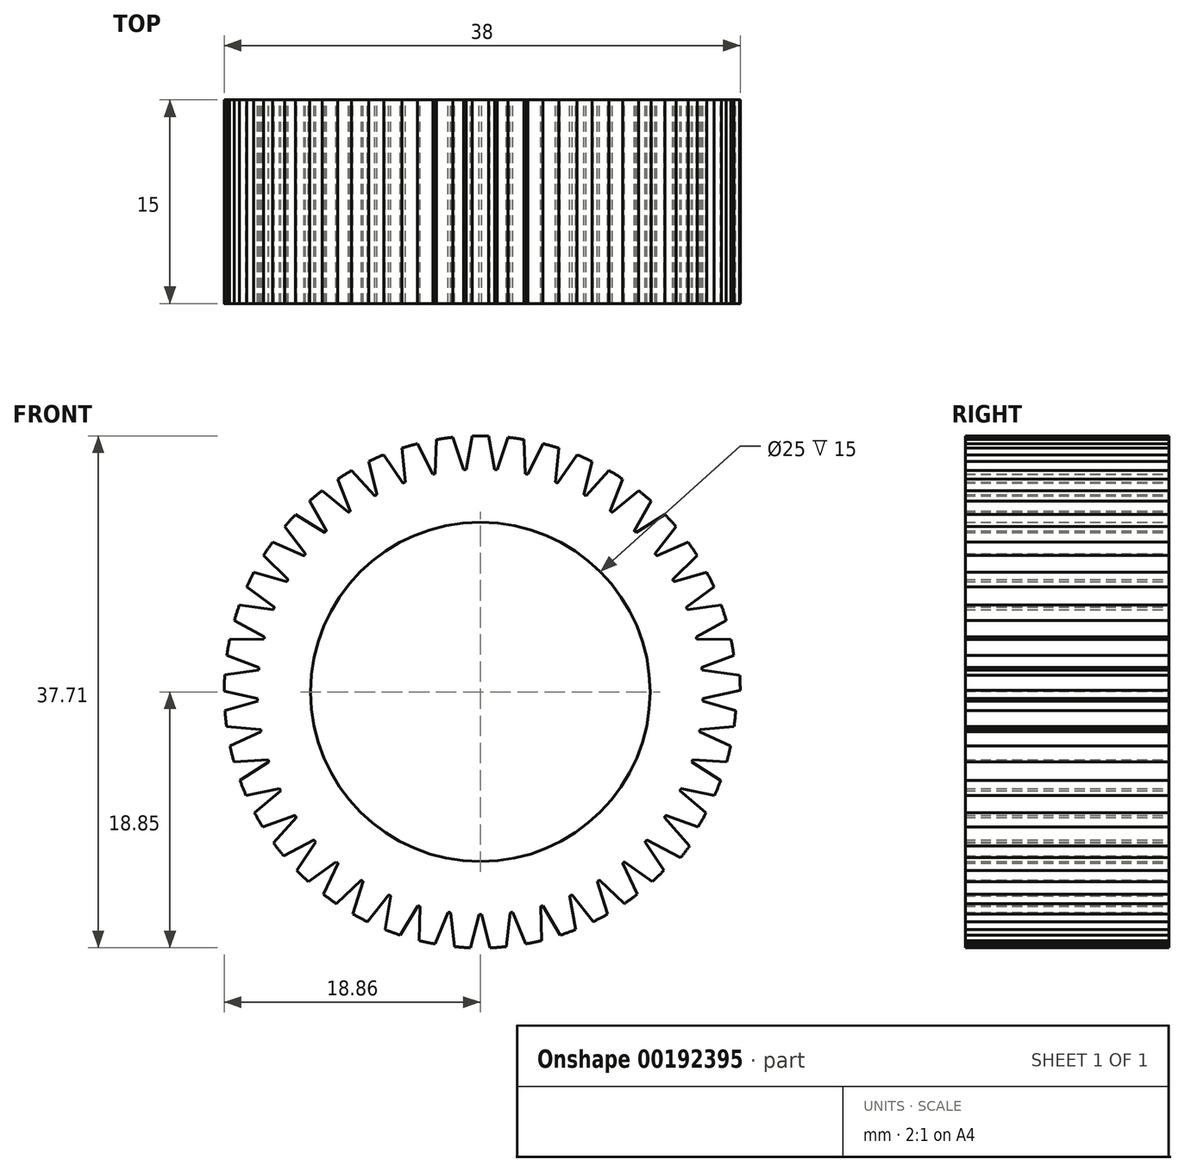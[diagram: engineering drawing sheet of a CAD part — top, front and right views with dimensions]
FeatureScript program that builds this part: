
annotation { "Feature Type Name" : "Feature", "Feature Type Description" : "" }
export const myFeature = defineFeature(function(context is Context, id is Id, definition is map)
    precondition{}
    {
        {
            var Q0;
            Q0=qCreatedBy(makeId("Front.planeOp"),FACE);
            var sketch = newSketch(context, id + "F0", { "sketchPlane" : qUnion([Q0])});
            skCircle(sketch, "E0", {"center": v(0, 0) * mm, "radius": 12.5 * mm});
            skLineSegment(sketch, "E1", {"start": v(-0.6, 18.85) * mm, "end": v(-1.05, 16.37) * mm});
            skLineSegment(sketch, "E2.MirrorCS", {"start": v(0.6, 18.85) * mm, "end": v(1.05, 16.37) * mm});
            skCircle(sketch, "E3", {"center": v(0, 0) * mm, "radius": 16.4 * mm});
            skLineSegment(sketch, "E4.1.1", {"start": v(-3.22, 18.58) * mm, "end": v(-3.32, 16.07) * mm});
            skLineSegment(sketch, "E4.1.2", {"start": v(-2.03, 18.75) * mm, "end": v(-1.23, 16.36) * mm});
            skLineSegment(sketch, "E4.2.1", {"start": v(-5.77, 17.96) * mm, "end": v(-5.53, 15.45) * mm});
            skLineSegment(sketch, "E4.2.2", {"start": v(-4.62, 18.29) * mm, "end": v(-3.5, 16.03) * mm});
            skLineSegment(sketch, "E5.4.3.0", {"start": v(-8.21, 16.98) * mm, "end": v(-7.62, 14.53) * mm});
            skLineSegment(sketch, "E5.7.3.0", {"start": v(-7.12, 17.46) * mm, "end": v(-5.7, 15.39) * mm});
            skLineSegment(sketch, "E5.4.4.0", {"start": v(-10.5, 15.67) * mm, "end": v(-9.57, 13.33) * mm});
            skLineSegment(sketch, "E5.7.4.0", {"start": v(-9.48, 16.3) * mm, "end": v(-7.78, 14.44) * mm});
            skLineSegment(sketch, "E5.4.5.0", {"start": v(-12.58, 14.06) * mm, "end": v(-11.33, 11.86) * mm});
            skLineSegment(sketch, "E5.7.5.0", {"start": v(-11.66, 14.83) * mm, "end": v(-9.72, 13.22) * mm});
            skLineSegment(sketch, "E5.4.6.0", {"start": v(-14.4, 12.17) * mm, "end": v(-12.87, 10.17) * mm});
            skLineSegment(sketch, "E5.7.6.0", {"start": v(-13.6, 13.06) * mm, "end": v(-11.46, 11.74) * mm});
            skLineSegment(sketch, "E5.4.7.0", {"start": v(-15.96, 10.04) * mm, "end": v(-14.16, 8.28) * mm});
            skLineSegment(sketch, "E5.7.7.0", {"start": v(-15.3, 11.04) * mm, "end": v(-12.98, 10.03) * mm});
            skLineSegment(sketch, "E5.4.8.0", {"start": v(-17.2, 7.73) * mm, "end": v(-15.18, 6.23) * mm});
            skLineSegment(sketch, "E5.7.8.0", {"start": v(-16.68, 8.8) * mm, "end": v(-14.25, 8.12) * mm});
            skLineSegment(sketch, "E5.4.9.0", {"start": v(-18.11, 5.26) * mm, "end": v(-15.9, 4.06) * mm});
            skLineSegment(sketch, "E5.7.9.0", {"start": v(-17.74, 6.4) * mm, "end": v(-15.25, 6.06) * mm});
            skLineSegment(sketch, "E5.4.10.0", {"start": v(-18.67, 2.68) * mm, "end": v(-16.3, 1.8) * mm});
            skLineSegment(sketch, "E5.7.10.0", {"start": v(-18.46, 3.86) * mm, "end": v(-15.94, 3.88) * mm});
            skLineSegment(sketch, "E5.4.11.0", {"start": v(-18.86, 0.06) * mm, "end": v(-16.4, -0.48) * mm});
            skLineSegment(sketch, "E5.7.11.0", {"start": v(-18.82, 1.26) * mm, "end": v(-16.33, 1.62) * mm});
            skLineSegment(sketch, "E5.4.12.0", {"start": v(-18.69, -2.57) * mm, "end": v(-16.17, -2.76) * mm});
            skLineSegment(sketch, "E5.7.12.0", {"start": v(-18.81, -1.38) * mm, "end": v(-16.4, -0.66) * mm});
            skLineSegment(sketch, "E5.4.13.0", {"start": v(-18.15, -5.14) * mm, "end": v(-15.63, -4.98) * mm});
            skLineSegment(sketch, "E5.7.13.0", {"start": v(-18.44, -3.98) * mm, "end": v(-16.14, -2.94) * mm});
            skLineSegment(sketch, "E5.4.14.0", {"start": v(-17.25, -7.62) * mm, "end": v(-14.79, -7.11) * mm});
            skLineSegment(sketch, "E5.7.14.0", {"start": v(-17.7, -6.5) * mm, "end": v(-15.58, -5.16) * mm});
            skLineSegment(sketch, "E5.4.15.0", {"start": v(-16.03, -9.94) * mm, "end": v(-13.65, -9.1) * mm});
            skLineSegment(sketch, "E5.7.15.0", {"start": v(-16.62, -8.9) * mm, "end": v(-14.7, -7.27) * mm});
            skLineSegment(sketch, "E5.4.16.0", {"start": v(-14.49, -12.08) * mm, "end": v(-12.25, -10.91) * mm});
            skLineSegment(sketch, "E5.7.16.0", {"start": v(-15.22, -11.13) * mm, "end": v(-13.55, -9.25) * mm});
            skLineSegment(sketch, "E5.4.17.0", {"start": v(-12.66, -13.98) * mm, "end": v(-10.62, -12.5) * mm});
            skLineSegment(sketch, "E5.7.17.0", {"start": v(-13.53, -13.14) * mm, "end": v(-12.13, -11.05) * mm});
            skLineSegment(sketch, "E5.4.18.0", {"start": v(-10.6, -15.6) * mm, "end": v(-8.77, -13.87) * mm});
            skLineSegment(sketch, "E5.7.18.0", {"start": v(-11.56, -14.9) * mm, "end": v(-10.48, -12.63) * mm});
            skLineSegment(sketch, "E5.4.19.0", {"start": v(-8.32, -16.93) * mm, "end": v(-6.76, -14.95) * mm});
            skLineSegment(sketch, "E5.7.19.0", {"start": v(-9.38, -16.36) * mm, "end": v(-8.62, -13.96) * mm});
            skLineSegment(sketch, "E6.4.20.0", {"start": v(-5.88, -17.92) * mm, "end": v(-4.6, -15.75) * mm});
            skLineSegment(sketch, "E6.7.20.0", {"start": v(-7, -17.5) * mm, "end": v(-6.6, -15.02) * mm});
            skLineSegment(sketch, "E6.4.21.0", {"start": v(-3.33, -18.56) * mm, "end": v(-2.37, -16.23) * mm});
            skLineSegment(sketch, "E6.7.21.0", {"start": v(-4.5, -18.31) * mm, "end": v(-4.43, -15.8) * mm});
            skLineSegment(sketch, "E6.4.22.0", {"start": v(-0.72, -18.85) * mm, "end": v(-0.1, -16.4) * mm});
            skLineSegment(sketch, "E6.7.22.0", {"start": v(-1.91, -18.76) * mm, "end": v(-2.2, -16.26) * mm});
            skLineSegment(sketch, "E6.4.23.0", {"start": v(1.91, -18.76) * mm, "end": v(2.2, -16.26) * mm});
            skLineSegment(sketch, "E6.7.23.0", {"start": v(0.72, -18.85) * mm, "end": v(0.1, -16.4) * mm});
            skLineSegment(sketch, "E6.4.24.0", {"start": v(4.5, -18.31) * mm, "end": v(4.43, -15.8) * mm});
            skLineSegment(sketch, "E6.7.24.0", {"start": v(3.33, -18.56) * mm, "end": v(2.37, -16.23) * mm});
            skLineSegment(sketch, "E6.4.25.0", {"start": v(7, -17.5) * mm, "end": v(6.6, -15.02) * mm});
            skLineSegment(sketch, "E6.7.25.0", {"start": v(5.88, -17.92) * mm, "end": v(4.6, -15.75) * mm});
            skLineSegment(sketch, "E6.4.26.0", {"start": v(9.38, -16.36) * mm, "end": v(8.62, -13.96) * mm});
            skLineSegment(sketch, "E6.7.26.0", {"start": v(8.32, -16.93) * mm, "end": v(6.76, -14.95) * mm});
            skLineSegment(sketch, "E6.4.27.0", {"start": v(11.56, -14.9) * mm, "end": v(10.48, -12.63) * mm});
            skLineSegment(sketch, "E6.7.27.0", {"start": v(10.6, -15.6) * mm, "end": v(8.77, -13.87) * mm});
            skLineSegment(sketch, "E6.4.28.0", {"start": v(13.53, -13.14) * mm, "end": v(12.13, -11.05) * mm});
            skLineSegment(sketch, "E6.7.28.0", {"start": v(12.66, -13.98) * mm, "end": v(10.62, -12.5) * mm});
            skArc(sketch, "E6.1.29.0", {"start": v(14.74, -12.21) * mm, "mid": v(15.08, -11.78) * mm, "end": v(15.41, -11.35) * mm});
            skLineSegment(sketch, "E6.4.29.0", {"start": v(15.41, -11.35) * mm, "end": v(13.55, -9.25) * mm});
            skLineSegment(sketch, "E6.7.29.0", {"start": v(14.74, -12.21) * mm, "end": v(12.25, -10.91) * mm});
            skLineSegment(sketch, "E6.4.30.0", {"start": v(16.62, -8.9) * mm, "end": v(14.7, -7.27) * mm});
            skLineSegment(sketch, "E6.7.30.0", {"start": v(16.03, -9.94) * mm, "end": v(13.65, -9.1) * mm});
            skLineSegment(sketch, "E6.4.31.0", {"start": v(17.7, -6.5) * mm, "end": v(15.58, -5.16) * mm});
            skLineSegment(sketch, "E6.7.31.0", {"start": v(17.25, -7.62) * mm, "end": v(14.79, -7.11) * mm});
            skLineSegment(sketch, "E6.4.32.0", {"start": v(18.44, -3.98) * mm, "end": v(16.14, -2.94) * mm});
            skLineSegment(sketch, "E6.7.32.0", {"start": v(18.15, -5.14) * mm, "end": v(15.63, -4.98) * mm});
            skLineSegment(sketch, "E6.4.33.0", {"start": v(18.81, -1.38) * mm, "end": v(16.4, -0.66) * mm});
            skLineSegment(sketch, "E6.7.33.0", {"start": v(18.69, -2.57) * mm, "end": v(16.17, -2.76) * mm});
            skArc(sketch, "E6.1.34.0", {"start": v(19.14, 0.12) * mm, "mid": v(19.13, 0.67) * mm, "end": v(19.1, 1.21) * mm});
            skLineSegment(sketch, "E6.4.34.0", {"start": v(19.1, 1.21) * mm, "end": v(16.33, 1.62) * mm});
            skLineSegment(sketch, "E6.7.34.0", {"start": v(19.14, 0.12) * mm, "end": v(16.4, -0.48) * mm});
            skLineSegment(sketch, "E6.4.35.0", {"start": v(18.46, 3.86) * mm, "end": v(15.94, 3.88) * mm});
            skLineSegment(sketch, "E6.7.35.0", {"start": v(18.67, 2.68) * mm, "end": v(16.3, 1.8) * mm});
            skLineSegment(sketch, "E6.4.36.0", {"start": v(17.74, 6.4) * mm, "end": v(15.25, 6.06) * mm});
            skLineSegment(sketch, "E6.7.36.0", {"start": v(18.11, 5.26) * mm, "end": v(15.9, 4.06) * mm});
            skLineSegment(sketch, "E6.4.37.0", {"start": v(16.68, 8.8) * mm, "end": v(14.25, 8.12) * mm});
            skLineSegment(sketch, "E6.7.37.0", {"start": v(17.2, 7.73) * mm, "end": v(15.18, 6.23) * mm});
            skLineSegment(sketch, "E6.4.38.0", {"start": v(15.3, 11.04) * mm, "end": v(12.98, 10.03) * mm});
            skLineSegment(sketch, "E6.7.38.0", {"start": v(15.96, 10.04) * mm, "end": v(14.16, 8.28) * mm});
            skLineSegment(sketch, "E6.4.39.0", {"start": v(13.6, 13.06) * mm, "end": v(11.46, 11.74) * mm});
            skLineSegment(sketch, "E6.7.39.0", {"start": v(14.4, 12.17) * mm, "end": v(12.87, 10.17) * mm});
            skLineSegment(sketch, "E6.4.40.0", {"start": v(11.66, 14.83) * mm, "end": v(9.72, 13.22) * mm});
            skLineSegment(sketch, "E6.7.40.0", {"start": v(12.58, 14.06) * mm, "end": v(11.33, 11.86) * mm});
            skLineSegment(sketch, "E6.4.41.0", {"start": v(9.48, 16.3) * mm, "end": v(7.78, 14.44) * mm});
            skLineSegment(sketch, "E6.7.41.0", {"start": v(10.5, 15.67) * mm, "end": v(9.57, 13.33) * mm});
            skLineSegment(sketch, "E6.4.42.0", {"start": v(7.12, 17.46) * mm, "end": v(5.7, 15.39) * mm});
            skLineSegment(sketch, "E6.7.42.0", {"start": v(8.21, 16.98) * mm, "end": v(7.62, 14.53) * mm});
            skLineSegment(sketch, "E6.4.43.0", {"start": v(4.62, 18.29) * mm, "end": v(3.5, 16.03) * mm});
            skLineSegment(sketch, "E6.7.43.0", {"start": v(5.77, 17.96) * mm, "end": v(5.53, 15.45) * mm});
            skLineSegment(sketch, "E6.4.44.0", {"start": v(2.03, 18.75) * mm, "end": v(1.23, 16.36) * mm});
            skLineSegment(sketch, "E6.7.44.0", {"start": v(3.22, 18.58) * mm, "end": v(3.32, 16.07) * mm});
            skArc(sketch, "E7", {"start": v(-9.48, 16.3) * mm, "mid": v(-10, 16) * mm, "end": v(-10.5, 15.67) * mm});
            skArc(sketch, "E8.trimOffspring", {"start": v(-11.66, 14.83) * mm, "mid": v(-12.12, 14.45) * mm, "end": v(-12.58, 14.06) * mm});
            skArc(sketch, "E9.trimOffspring", {"start": v(-13.6, 13.06) * mm, "mid": v(-14.02, 12.62) * mm, "end": v(-14.4, 12.17) * mm});
            skArc(sketch, "E10.trimOffspring", {"start": v(-15.3, 11.04) * mm, "mid": v(-15.64, 10.55) * mm, "end": v(-15.96, 10.04) * mm});
            skArc(sketch, "E11.trimOffspring", {"start": v(-16.68, 8.8) * mm, "mid": v(-16.95, 8.27) * mm, "end": v(-17.2, 7.73) * mm});
            skArc(sketch, "E12.trimOffspring", {"start": v(-17.74, 6.4) * mm, "mid": v(-17.94, 5.83) * mm, "end": v(-18.11, 5.26) * mm});
            skArc(sketch, "E13.trimOffspring", {"start": v(-18.46, 3.86) * mm, "mid": v(-18.57, 3.28) * mm, "end": v(-18.67, 2.68) * mm});
            skArc(sketch, "E14.trimOffspring", {"start": v(-18.82, 1.26) * mm, "mid": v(-18.85, 0.66) * mm, "end": v(-18.86, 0.06) * mm});
            skArc(sketch, "E15.trimOffspring", {"start": v(-18.81, -1.38) * mm, "mid": v(-18.76, -1.97) * mm, "end": v(-18.69, -2.57) * mm});
            skArc(sketch, "E16.trimOffspring", {"start": v(-18.44, -3.98) * mm, "mid": v(-18.3, -4.56) * mm, "end": v(-18.15, -5.14) * mm});
            skArc(sketch, "E17.trimOffspring", {"start": v(-17.7, -6.5) * mm, "mid": v(-17.49, -7.07) * mm, "end": v(-17.25, -7.62) * mm});
            skArc(sketch, "E18.trimOffspring", {"start": v(-16.62, -8.9) * mm, "mid": v(-16.33, -9.43) * mm, "end": v(-16.03, -9.94) * mm});
            skArc(sketch, "E19.trimOffspring", {"start": v(-15.22, -11.13) * mm, "mid": v(-14.86, -11.61) * mm, "end": v(-14.49, -12.08) * mm});
            skArc(sketch, "E20.trimOffspring", {"start": v(-13.53, -13.14) * mm, "mid": v(-13.1, -13.57) * mm, "end": v(-12.66, -13.98) * mm});
            skArc(sketch, "E21.trimOffspring", {"start": v(-11.56, -14.9) * mm, "mid": v(-11.09, -15.26) * mm, "end": v(-10.6, -15.6) * mm});
            skArc(sketch, "E22.trimOffspring", {"start": v(-9.38, -16.36) * mm, "mid": v(-8.85, -16.65) * mm, "end": v(-8.32, -16.93) * mm});
            skArc(sketch, "E23.trimOffspring", {"start": v(-7, -17.5) * mm, "mid": v(-6.45, -17.72) * mm, "end": v(-5.88, -17.92) * mm});
            skArc(sketch, "E24.trimOffspring", {"start": v(-4.5, -18.31) * mm, "mid": v(-3.92, -18.45) * mm, "end": v(-3.33, -18.56) * mm});
            skArc(sketch, "E25.trimOffspring", {"start": v(-1.91, -18.76) * mm, "mid": v(-1.32, -18.81) * mm, "end": v(-0.72, -18.85) * mm});
            skArc(sketch, "E26.trimOffspring", {"start": v(0.72, -18.85) * mm, "mid": v(1.32, -18.81) * mm, "end": v(1.91, -18.76) * mm});
            skArc(sketch, "E27.trimOffspring", {"start": v(3.33, -18.56) * mm, "mid": v(3.92, -18.45) * mm, "end": v(4.5, -18.31) * mm});
            skArc(sketch, "E28.trimOffspring", {"start": v(5.88, -17.92) * mm, "mid": v(6.45, -17.72) * mm, "end": v(7, -17.5) * mm});
            skArc(sketch, "E29.trimOffspring", {"start": v(8.32, -16.93) * mm, "mid": v(8.85, -16.65) * mm, "end": v(9.38, -16.36) * mm});
            skArc(sketch, "E30.trimOffspring", {"start": v(10.6, -15.6) * mm, "mid": v(11.09, -15.26) * mm, "end": v(11.56, -14.9) * mm});
            skArc(sketch, "E31.trimOffspring", {"start": v(12.66, -13.98) * mm, "mid": v(13.1, -13.57) * mm, "end": v(13.53, -13.14) * mm});
            skArc(sketch, "E32.trimOffspring", {"start": v(16.03, -9.94) * mm, "mid": v(16.33, -9.43) * mm, "end": v(16.62, -8.9) * mm});
            skArc(sketch, "E33.trimOffspring", {"start": v(17.25, -7.62) * mm, "mid": v(17.49, -7.07) * mm, "end": v(17.7, -6.5) * mm});
            skArc(sketch, "E34.trimOffspring", {"start": v(18.15, -5.14) * mm, "mid": v(18.3, -4.56) * mm, "end": v(18.44, -3.98) * mm});
            skArc(sketch, "E35.trimOffspring", {"start": v(18.69, -2.57) * mm, "mid": v(18.76, -1.97) * mm, "end": v(18.81, -1.38) * mm});
            skArc(sketch, "E36.trimOffspring", {"start": v(18.67, 2.68) * mm, "mid": v(18.57, 3.28) * mm, "end": v(18.46, 3.86) * mm});
            skArc(sketch, "E37.trimOffspring", {"start": v(17.2, 7.73) * mm, "mid": v(16.95, 8.27) * mm, "end": v(16.68, 8.8) * mm});
            skArc(sketch, "E38.trimOffspring", {"start": v(18.11, 5.26) * mm, "mid": v(17.94, 5.83) * mm, "end": v(17.74, 6.4) * mm});
            skArc(sketch, "E39.trimOffspring", {"start": v(15.96, 10.04) * mm, "mid": v(15.64, 10.55) * mm, "end": v(15.3, 11.04) * mm});
            skArc(sketch, "E40.trimOffspring", {"start": v(14.4, 12.17) * mm, "mid": v(14.02, 12.62) * mm, "end": v(13.6, 13.06) * mm});
            skArc(sketch, "E41.trimOffspring", {"start": v(12.58, 14.06) * mm, "mid": v(12.12, 14.45) * mm, "end": v(11.66, 14.83) * mm});
            skArc(sketch, "E42.trimOffspring", {"start": v(10.5, 15.67) * mm, "mid": v(10, 16) * mm, "end": v(9.48, 16.3) * mm});
            skArc(sketch, "E43.trimOffspring", {"start": v(8.21, 16.98) * mm, "mid": v(7.67, 17.23) * mm, "end": v(7.12, 17.46) * mm});
            skArc(sketch, "E44.trimOffspring", {"start": v(5.77, 17.96) * mm, "mid": v(5.2, 18.13) * mm, "end": v(4.62, 18.29) * mm});
            skArc(sketch, "E45.trimOffspring", {"start": v(3.22, 18.58) * mm, "mid": v(2.62, 18.68) * mm, "end": v(2.03, 18.75) * mm});
            skArc(sketch, "E46.trimOffspring", {"start": v(0.6, 18.85) * mm, "mid": v(0, 18.86) * mm, "end": v(-0.6, 18.85) * mm});
            skArc(sketch, "E47.trimOffspring", {"start": v(-2.03, 18.75) * mm, "mid": v(-2.62, 18.68) * mm, "end": v(-3.22, 18.58) * mm});
            skArc(sketch, "E48.trimOffspring", {"start": v(-4.62, 18.29) * mm, "mid": v(-5.2, 18.13) * mm, "end": v(-5.77, 17.96) * mm});
            skArc(sketch, "E49.trimOffspring", {"start": v(-7.12, 17.46) * mm, "mid": v(-7.67, 17.23) * mm, "end": v(-8.21, 16.98) * mm});
            skSolve(sketch);
        }
        {
            var Q0;
            Q0 = qSketchRegion(id + "F0", true);
            extrude(context, id + "F1", {"entities" : qUnion([Q0]), "depth" : 15 * mm});
        }
    });
